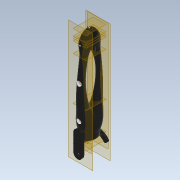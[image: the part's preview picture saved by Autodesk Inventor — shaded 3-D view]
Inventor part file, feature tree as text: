
AUTODESK INVENTOR PART (.ipt)
format: ipt  version: 2020.2 (Build 242310000, 310)  size: 636,416 bytes
history: native  units: mm
features: sketch x22, extrude x15, plane x12, loft x2, fillet x1
ambient origin geometry x8: Origin, YZ Plane, XZ Plane, XY Plane, X Axis, Y Axis, Z Axis, Center Point
bodies: Solid1 (feature_tree)
feature tree (52):
  plane  "Work Plane1"
  plane  "Work Plane4"
  plane  "Work Plane5"
  sketch  "Sketch7"  dims[d35=20.5mm d36=50.0mm d37=0.0mm]
  sketch  "Sketch1"  dims[d0=-30.0mm d1=50.0mm]
  sketch  "Sketch2"  dims[d2=100.0mm d3=35.0mm d5=15.0mm]
  sketch  "Sketch4"  dims[d24=0.0mm d25=90.0deg d26=200.0mm d27=90.0deg]
  sketch  "Sketch3"  dims[d6=0.0mm d7=90.0deg d8=0.0mm d9=90.0deg d10=0.0mm d11=90.0deg d14=0.0mm d15=90.0deg d16=0.0mm d17=90.0deg d18=0.0mm d19=90.0deg d22=200.0mm d23=90.0deg]
  sketch  "Sketch5"  dims[d28=200.0mm d29=90.0deg d30=0.0mm d31=90.0deg]
  sketch  "Sketch6"  dims[d32=200.0mm d33=90.0deg d34=-10.0mm]
  loft  "Loft1"
  loft  "Loft2"
  plane  "Work Plane6"
  extrude  "Extrusion1"  Depth=200.0mm TaperAngle=90.0deg
  extrude  "Extrusion2"  Depth=200.0mm TaperAngle=90.0deg
  extrude  "Extrusion3"  TaperAngle=0.0deg  [1 undecoded]
  extrude  "Extrusion4"  [1 undecoded]
  plane  "Work Plane7"
  extrude  "Extrusion5"  Depth=50.0mm TaperAngle=0.0deg
  extrude  "Extrusion6"  Depth=2.0mm TaperAngle=0.0deg
  extrude  "Extrusion7"  Depth=20.006mm TaperAngle=0.0deg
  plane  "Work Plane8"
  extrude  "Extrusion8"  Depth=15.0mm
  plane  "Work Plane9"
  extrude  "Extrusion9"  Depth=2.5mm
  fillet  "Fillet1"  Radius=205.006mm
  plane  "Work Plane11"
  extrude  "Extrusion11"  Depth=5.0mm
  extrude  "Extrusion12"  Depth=19.927mm TaperAngle=0.0deg
  plane  "Work Plane12"
  plane  "Work Plane13"
  sketch  "Sketch20"  dims[d66=30.0mm]
  extrude  "Extrusion13"  Depth=19.927mm TaperAngle=0.0deg
  extrude  "Extrusion14"  Depth=7.0mm
  extrude  "Extrusion15"  Depth=15.0mm
  extrude  "Extrusion16"  [1 undecoded]
  plane  "Work Plane2"
  plane  "Work Plane3"
  sketch  "Sketch8"  dims[d38=7.0mm d39=2.0mm d40=0.0mm]
  sketch  "Sketch9"  dims[d41=3.5mm d42=20.006mm d43=0.0mm]
  sketch  "Sketch10"  dims[d44=7.5mm d45=15.0mm]
  sketch  "Sketch11"  dims[d46=2.5mm d47=2.5mm d48=205.006mm d49=0.0mm]
  sketch  "Sketch12"  dims[d50=5.0mm d51=5.0mm]
  sketch  "Sketch13"  dims[d52=5.0mm d53=19.927mm d54=0.0mm]
  sketch  "Sketch14"  dims[d55=10.5mm d56=19.927mm d57=0.0mm]
  sketch  "Sketch15"  dims[d58=5.0mm d59=7.0mm]
  sketch  "Sketch16"  dims[d60=14.005mm d61=0.0mm d62=15.0mm]
  sketch  "Sketch18"  dims[d63=20.0mm d64=0.0mm d65=-20.0mm]
  sketch  "Sketch21"  dims[d67=62.5mm]
  sketch  "Sketch22"  dims[d68=45.0mm]
  sketch  "Sketch23"  dims[d69=5.0mm d70=0.0mm]
  sketch  "Sketch24"  dims[d71=3.5mm d74=3.0mm d75=3.0mm d76=27.5mm d77=27.5mm d78=45.0deg d79=45.0deg d94=37.0mm d95=8.0mm d96=20.0mm d97=20.0mm d98=5.0mm d99=0.0mm d100=20.0mm d101=15.0mm d102=0.0mm d103=20.0mm d104=-20.0mm d105=25.0mm d106=10.5mm d107=150.0mm d108=10.5mm d109=47.494mm d110=0.0mm d111=75.0mm d112=10.5mm d113=10.5mm d114=7.494mm d115=0.0mm d116=3.0mm d117=150.0mm d118=3.0mm d119=11.003mm d120=0.0mm d121=3.0mm d122=10.0mm d123=0.0mm d124=15.0mm]
note: 3 required parameter values undecoded (feature->parameter linkage not recoverable at this tier; creation-order binding heuristic only, values carry confidence <= 0.55)
